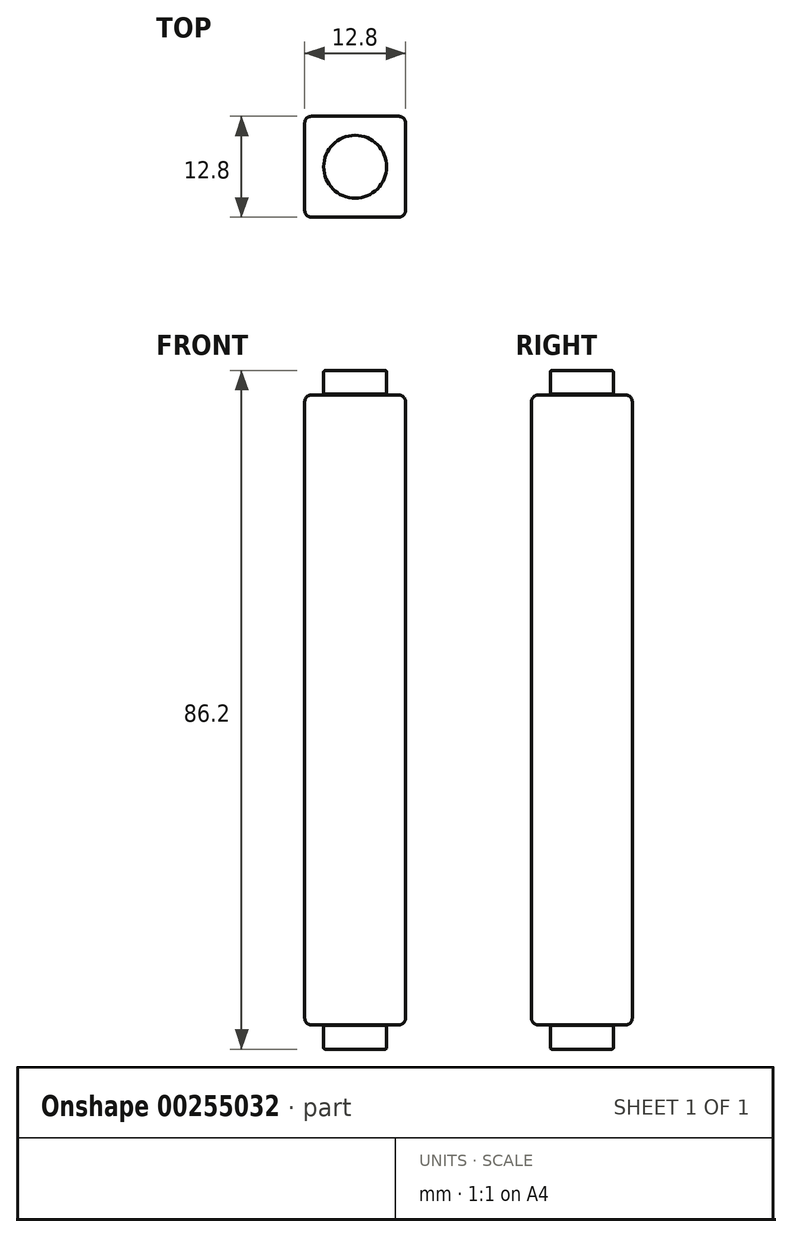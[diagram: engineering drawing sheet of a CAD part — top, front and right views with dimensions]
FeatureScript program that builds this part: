
annotation { "Feature Type Name" : "Feature", "Feature Type Description" : "" }
export const myFeature = defineFeature(function(context is Context, id is Id, definition is map)
    precondition{}
    {
        {
            var Q0;
            Q0=qCreatedBy(makeId("Top.planeOp"),FACE);
            var sketch = newSketch(context, id + "F0", { "sketchPlane" : qUnion([Q0])});
            skLineSegment(sketch, "E0.bottom", {"start": v(6.4, -6.4) * mm, "end": v(-6.4, -6.4) * mm});
            skLineSegment(sketch, "E0.top", {"start": v(6.4, 6.4) * mm, "end": v(-6.4, 6.4) * mm});
            skLineSegment(sketch, "E0.left", {"start": v(6.4, -6.4) * mm, "end": v(6.4, 6.4) * mm});
            skLineSegment(sketch, "E0.right", {"start": v(-6.4, -6.4) * mm, "end": v(-6.4, 6.4) * mm});
            skPoint(sketch, "E0.middle", {"position": v(0, 0) * mm});
            skSolve(sketch);
        }
        {
            var Q0;
            Q0=qSketchRegion(id+"F0",true);
            extrude(context, id + "F1", {"entities" : qUnion([Q0]), "depth" : 80 * mm});
        }
        {
            var Q0;
            Q0=makeQuery(id+"F1.opExtrude","SWEPT_EDGE",EDGE,{"disambiguationData":[OSD([sQuery(id+"F0.wireOp",EDGE,"E0.bottom"),sQuery(id+"F0.wireOp",EDGE,"E0.left")])]});
            var Q1;
            Q1=makeQuery(id+"F1.opExtrude","SWEPT_EDGE",EDGE,{"disambiguationData":[OSD([sQuery(id+"F0.wireOp",EDGE,"E0.bottom"),sQuery(id+"F0.wireOp",EDGE,"E0.right")])]});
            var Q2;
            Q2=makeQuery(id+"F1.opExtrude","SWEPT_EDGE",EDGE,{"disambiguationData":[OSD([sQuery(id+"F0.wireOp",EDGE,"E0.top"),sQuery(id+"F0.wireOp",EDGE,"E0.left")])]});
            var Q3;
            Q3=makeQuery(id+"F1.opExtrude","SWEPT_EDGE",EDGE,{"disambiguationData":[OSD([sQuery(id+"F0.wireOp",EDGE,"E0.top"),sQuery(id+"F0.wireOp",EDGE,"E0.right")])]});
            var Q4;
            Q4=makeQuery(id+"F1.opExtrude","CAP_FACE",FACE,{"disambiguationData":[OSD([sQuery(id+"F0.wireOp",EDGE,"E0.bottom"),sQuery(id+"F0.wireOp",EDGE,"E0.top"),sQuery(id+"F0.wireOp",EDGE,"E0.left"),sQuery(id+"F0.wireOp",EDGE,"E0.right")])],"isStart":true});
            var Q5;
            Q5=makeQuery(id+"F1.opExtrude","CAP_FACE",FACE,{"disambiguationData":[OSD([sQuery(id+"F0.wireOp",EDGE,"E0.bottom"),sQuery(id+"F0.wireOp",EDGE,"E0.top"),sQuery(id+"F0.wireOp",EDGE,"E0.left"),sQuery(id+"F0.wireOp",EDGE,"E0.right")])],"isStart":false});
            fillet(context, id + "F2", {"entities" : qUnion([Q0, Q1, Q2, Q3, Q4, Q5]), "radius" : 0.8 * mm, "tangentPropagation" : true, "allowEdgeOverflow" : false});
        }
        {
            var Q0;
            Q0=makeQuery(id+"F1.opExtrude","CAP_FACE",FACE,{"disambiguationData":[OSD([sQuery(id+"F0.wireOp",EDGE,"E0.bottom"),sQuery(id+"F0.wireOp",EDGE,"E0.top"),sQuery(id+"F0.wireOp",EDGE,"E0.left"),sQuery(id+"F0.wireOp",EDGE,"E0.right")])],"isStart":true});
            var sketch = newSketch(context, id + "F3", { "sketchPlane" : qUnion([Q0])});
            skCircle(sketch, "E1", {"center": v(0, 0) * mm, "radius": 4 * mm});
            skSolve(sketch);
        }
        {
            var Q0;
            Q0=qSketchRegion(id+"F3",true);
            extrude(context, id + "F4", {"entities" : qUnion([Q0]), "depth" : 3.1 * mm, "hasSecondDirection" : true, "secondDirectionOppositeDirection" : false, "secondDirectionDepth" : 0.1 * mm});
        }
        {
            var Q0;
            Q0=makeQuery(id+"F4.opExtrude","CAP_EDGE",EDGE,{"disambiguationData":[OSD([sQuery(id+"F3.wireOp",EDGE,"E1")])],"isStart":false});
            var Q1;
            Q1=makeQuery(id+"F4.opExtrude","CAP_EDGE",EDGE,{"disambiguationData":[OSD([sQuery(id+"F3.wireOp",EDGE,"E1")])],"isStart":true});
            fillet(context, id + "F5", {"entities" : qUnion([Q0, Q1]), "radius" : 0.2 * mm, "tangentPropagation" : true, "allowEdgeOverflow" : false});
        }
        {
            var Q0;
            Q0=makeQuery(id+"F1.opExtrude","CAP_FACE",FACE,{"disambiguationData":[OSD([sQuery(id+"F0.wireOp",EDGE,"E0.bottom"),sQuery(id+"F0.wireOp",EDGE,"E0.top"),sQuery(id+"F0.wireOp",EDGE,"E0.left"),sQuery(id+"F0.wireOp",EDGE,"E0.right")])],"isStart":false});
            var sketch = newSketch(context, id + "F6", { "sketchPlane" : qUnion([Q0])});
            skCircle(sketch, "E2", {"center": v(0, 0) * mm, "radius": 4 * mm});
            skSolve(sketch);
        }
        {
            var Q0;
            Q0=qSketchRegion(id+"F6",true);
            extrude(context, id + "F7", {"entities" : qUnion([Q0]), "depth" : 3.1 * mm, "hasSecondDirection" : true, "secondDirectionOppositeDirection" : false, "secondDirectionDepth" : 0.1 * mm});
        }
        {
            var Q0;
            Q0=makeQuery(id+"F7.opExtrude","CAP_EDGE",EDGE,{"disambiguationData":[OSD([sQuery(id+"F6.wireOp",EDGE,"E2")])],"isStart":false});
            var Q1;
            Q1=makeQuery(id+"F7.opExtrude","CAP_EDGE",EDGE,{"disambiguationData":[OSD([sQuery(id+"F6.wireOp",EDGE,"E2")])],"isStart":true});
            fillet(context, id + "F8", {"entities" : qUnion([Q0, Q1]), "radius" : 0.2 * mm, "tangentPropagation" : true, "allowEdgeOverflow" : false});
        }
    });
